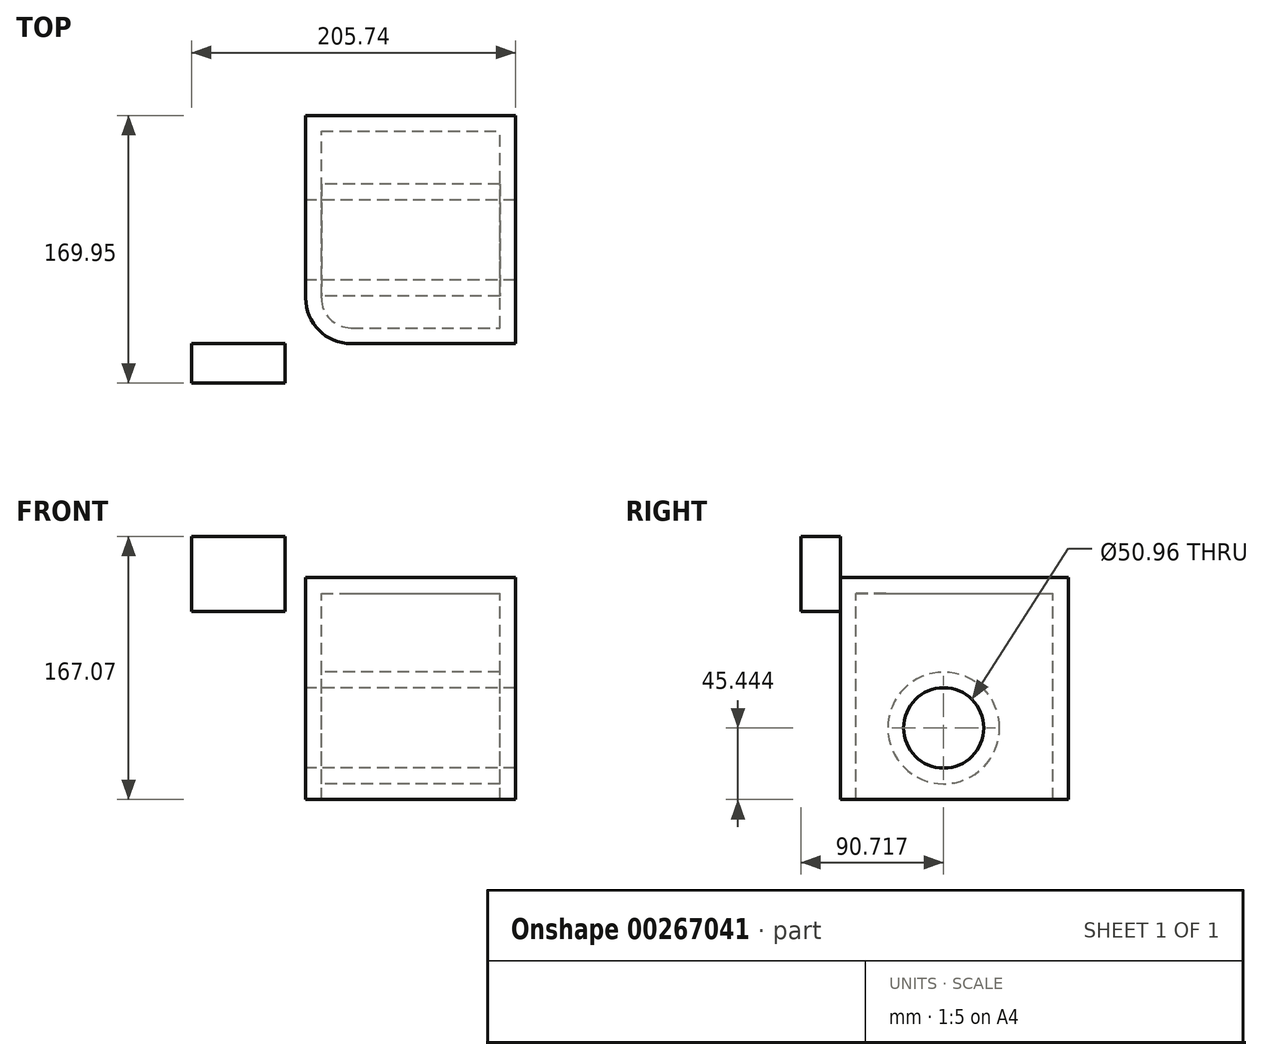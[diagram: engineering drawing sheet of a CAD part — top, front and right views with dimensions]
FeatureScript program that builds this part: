
annotation { "Feature Type Name" : "Feature", "Feature Type Description" : "" }
export const myFeature = defineFeature(function(context is Context, id is Id, definition is map)
    precondition{}
    {
        {
            var Q0;
            Q0=qCreatedBy(makeId("Top.planeOp"),FACE);
            var sketch = newSketch(context, id + "F0", { "sketchPlane" : qUnion([Q0])});
            skLineSegment(sketch, "E0.bottom", {"start": v(0, 0) * mm, "end": v(133.3, 0) * mm});
            skLineSegment(sketch, "E0.top", {"start": v(0, 144.95) * mm, "end": v(133.3, 144.95) * mm});
            skLineSegment(sketch, "E0.left", {"start": v(0, 0) * mm, "end": v(0, 144.95) * mm});
            skLineSegment(sketch, "E0.right", {"start": v(133.3, 0) * mm, "end": v(133.3, 144.95) * mm});
            skSolve(sketch);
        }
        {
            var Q0;
            Q0 = qSketchRegion(id + "F0", true);
            extrude(context, id + "F1", {"entities" : qUnion([Q0]), "oppositeDirection" : true, "depth" : 141 * mm});
        }
        {
            var Q0;
            Q0=makeQuery(id+"F1.opExtrude","SWEPT_FACE",FACE,{"disambiguationData":[OSD([sQuery(id+"F0.wireOp",EDGE,"E0.left")])]});
            var sketch = newSketch(context, id + "F2", { "sketchPlane" : qUnion([Q0])});
            skCircle(sketch, "E1", {"center": v(-65.72, -95.56) * mm, "radius": 25.48 * mm});
            skSolve(sketch);
        }
        {
            var Q0;
            Q0 = qSketchRegion(id + "F2", true);
            extrude(context, id + "F3", {"entities" : qUnion([Q0]), "operationType" : NewBodyOperationType.REMOVE, "endBound" : BoundingType.THROUGH_ALL, "oppositeDirection" : true, "depth" : 25 * mm});
        }
        {
            var Q0;
            Q0=makeQuery(id+"F1.opExtrude","SWEPT_EDGE",EDGE,{"disambiguationData":[OSD([sQuery(id+"F0.wireOp",EDGE,"E0.bottom"),sQuery(id+"F0.wireOp",EDGE,"E0.left")])]});
            fillet(context, id + "F4", {"entities" : qUnion([Q0]), "radius" : 28.97 * mm, "tangentPropagation" : true, "allowEdgeOverflow" : false});
        }
        {
            var Q0;
            Q0=makeQuery(id+"F1.opExtrude","CAP_FACE",FACE,{"disambiguationData":[OSD([sQuery(id+"F0.wireOp",EDGE,"E0.bottom"),sQuery(id+"F0.wireOp",EDGE,"E0.top"),sQuery(id+"F0.wireOp",EDGE,"E0.left"),sQuery(id+"F0.wireOp",EDGE,"E0.right")])],"isStart":false});
            shell(context, id + "F5", {"entities" : qUnion([Q0]), "thickness" : 10 * mm});
        }
        {
            var Q0;
            Q0=qCreatedBy(makeId("Front.planeOp"),FACE);
            var sketch = newSketch(context, id + "F6", { "sketchPlane" : qUnion([Q0])});
            skLineSegment(sketch, "E2.bottom", {"start": v(-72.43, 26.07) * mm, "end": v(-13.08, 26.07) * mm});
            skLineSegment(sketch, "E2.top", {"start": v(-72.43, -21.54) * mm, "end": v(-13.08, -21.54) * mm});
            skLineSegment(sketch, "E2.left", {"start": v(-72.43, 26.07) * mm, "end": v(-72.43, -21.54) * mm});
            skLineSegment(sketch, "E2.right", {"start": v(-13.08, 26.07) * mm, "end": v(-13.08, -21.54) * mm});
            skSolve(sketch);
        }
        {
            var Q0;
            Q0 = qSketchRegion(id + "F6", true);
            extrude(context, id + "F7", {"entities" : qUnion([Q0]), "depth" : 25 * mm});
        }
    });
